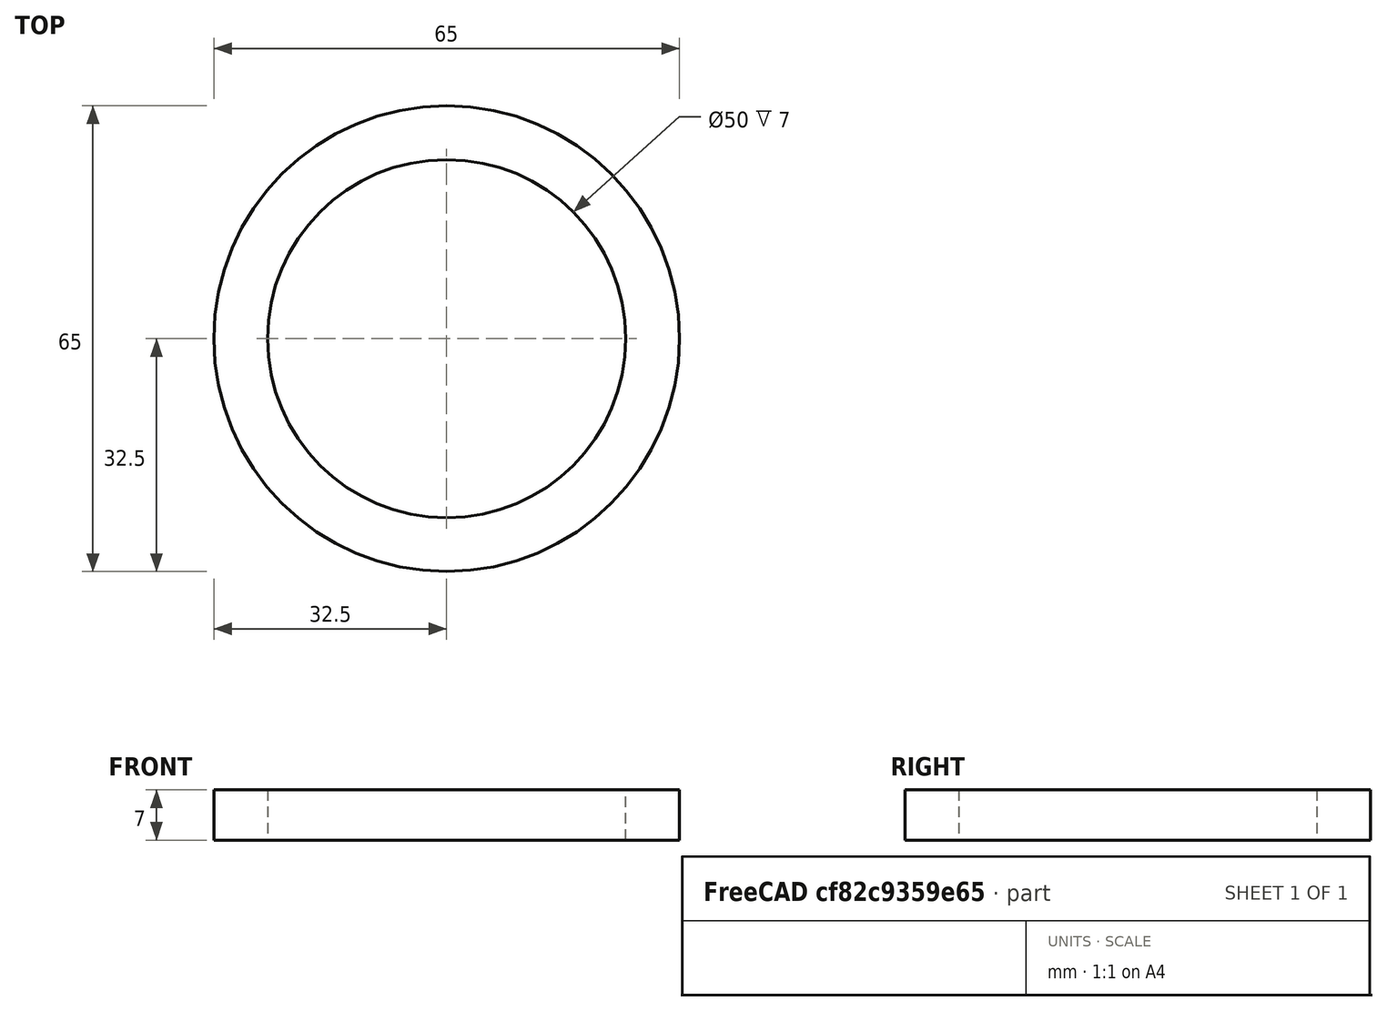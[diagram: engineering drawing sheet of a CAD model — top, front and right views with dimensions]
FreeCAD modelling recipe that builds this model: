
FCSTD DOCUMENT  (FreeCAD 0.19R24276 (Git))
Label: BALL-6810
License: All rights reserved
LicenseURL: http://en.wikipedia.org/wiki/All_rights_reserved
objects: Sketcher::SketchObject×1, PartDesign::Pad×1, PartDesign::Body×1, PartDesign::CoordinateSystem×1, App::Part×1
note: 5 computed .brp shape members not serialized (recipe doc carries the construction recipe); baked Part::Feature solids carry a one-line shape summary decoded from their .brp

FEATURE [Sketcher::SketchObject] Sketch
  FullyConstrained = true
  MapMode = 5
  Support = -> [XY_Plane]
  sketch-geometry (2):
    g0: Circle CenterX=0 CenterY=0 CenterZ=0 NormalX=0 NormalY=0 NormalZ=1 AngleXU=0 Radius=25
    g1: Circle CenterX=0 CenterY=0 CenterZ=0 NormalX=0 NormalY=0 NormalZ=1 AngleXU=0 Radius=32.5
  constraints (4):
    c: Coincident(g0,g-1)
    c: Coincident(g1,g0)
    c: Diameter(g0) = 50
    c: Diameter(g1) = 65
FEATURE [PartDesign::Pad] Pad
  Direction = (1,1,1)
  Length = 7
  Length2 = 100
  Profile = -> Sketch
  Refine = true
  Type = 0
FEATURE [PartDesign::Body] Body
  Group = -> [Sketch,Pad]
  Origin = -> Origin
  Tip = -> Pad
FEATURE [PartDesign::CoordinateSystem] LCS_0
  AttacherType = Attacher::AttachEngine3D
  MapMode = 2
  Support = -> [X_Axis001]
FEATURE [App::Part] Part
  Group = -> [LCS_0,Body]
  Origin = -> Origin001
